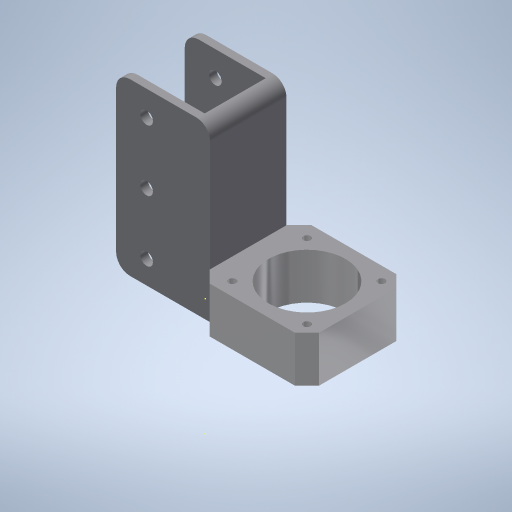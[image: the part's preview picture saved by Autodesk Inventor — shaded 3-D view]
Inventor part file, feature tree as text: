
AUTODESK INVENTOR PART (.ipt)
format: ipt  version: 2024 (Build 280153000, 153)  size: 638,464 bytes
history: native  units: mm
features: extrude x28, sketch x25, projected_geometry x17, fillet x5, chamfer x3
ambient origin geometry x8: Origin, YZ Plane, XZ Plane, XY Plane, X Axis, Y Axis, Z Axis, Center Point
bodies: Solid1 (feature_tree)
feature tree (78):
  extrude  "Extrusion1"  Depth=5.0mm
  fillet  "Fillet1"  Radius=5.0mm
  extrude  "Extrusion2"  Depth=21.1mm
  fillet  "Fillet2"  Radius=3.0mm
  extrude  "Extrusion3"  Depth=3.0mm
  extrude  "Extrusion4"  Depth=31.0mm
  extrude  "Extrusion5"  Depth=31.0mm
  fillet  "Fillet3"  Radius=31.0mm
  extrude  "Extrusion6"  Depth=5.6mm
  fillet  "Fillet4"  Radius=9.8mm
  extrude  "Extrusion7"  Depth=31.0mm TaperAngle=0.0deg
  sketch  "Sketch8"  dims[d14=3.0mm d15=3.0mm]
  extrude  "Extrusion8"  Depth=7.75mm TaperAngle=0.0deg
  extrude  "Extrusion9"  Depth=0.6mm TaperAngle=0.0deg
  extrude  "Extrusion10"  Depth=2.2mm TaperAngle=0.0deg
  extrude  "Extrusion11"  Depth=22.5mm TaperAngle=0.0deg
  extrude  "Extrusion12"  Depth=5.6mm
  extrude  "Extrusion13"  Depth=5.6mm
  extrude  "Extrusion14"  Depth=42.2mm
  chamfer  "Chamfer1"  Distance=6.35mm
  sketch  "Sketch16"  dims[d39=0.5mm d40=22.5mm d41=0.0mm]
  extrude  "Extrusion15"  Depth=98.4mm TaperAngle=0.0deg
  extrude  "Extrusion16"  Depth=16.9926mm TaperAngle=0.0deg
  extrude  "Extrusion17"  Depth=3.9926mm TaperAngle=0.0deg
  extrude  "Extrusion18"  Depth=8.4074mm
  extrude  "Extrusion19"  Depth=3.175mm
  extrude  "Extrusion20"  Depth=39.1mm TaperAngle=0.0deg
  extrude  "Extrusion21"  Depth=39.1mm TaperAngle=0.0deg
  extrude  "Extrusion22"  Depth=25.8mm TaperAngle=0.0deg
  extrude  "Extrusion23"  Depth=51.95mm TaperAngle=0.0deg
  extrude  "Extrusion24"  Depth=10.3886mm
  extrude  "Extrusion25"  Depth=25.4mm
  extrude  "Extrusion26"  Depth=25.4mm
  extrude  "Extrusion27"  Depth=5.75mm
  extrude  "Extrusion28"  Depth=5.75mm
  chamfer  "Chamfer2"  Distance=133.45mm
  chamfer  "Chamfer3"  Distance=6.35mm
  fillet  "Fillet7"  Radius=6.35mm
  sketch  "Sketch1"  dims[d8=5.0mm d9=5.0mm d10=5.0mm]
  sketch  "Sketch7"  dims[d11=21.1mm d12=21.1mm d13=3.0mm]
  projected_geometry  "Projected Loop1"
  sketch  "Sketch9"  dims[d16=3.0mm d17=31.0mm]
  sketch  "Sketch10"  dims[d18=31.0mm d19=31.0mm d20=31.0mm]
  projected_geometry  "Projected Loop2"
  projected_geometry  "Projected Loop3"
  sketch  "Sketch11"  dims[d21=5.6mm d22=5.6mm d23=9.8mm d24=0.0mm]
  sketch  "Sketch12"  dims[d25=0.25mm d26=31.0mm d27=0.0mm]
  projected_geometry  "Projected Loop4"
  projected_geometry  "Projected Loop5"
  sketch  "Sketch13"  dims[d28=0.25mm d29=7.75mm d30=0.0mm]
  projected_geometry  "Projected Loop6"
  projected_geometry  "Projected Loop7"
  sketch  "Sketch14"  dims[d31=32.0mm d33=0.6mm d34=0.0mm]
  sketch  "Sketch15"  dims[d35=22.0mm d37=2.2mm d38=0.0mm]
  projected_geometry  "Projected Loop8"
  projected_geometry  "Projected Loop9"
  projected_geometry  "Projected Loop10"
  projected_geometry  "Projected Loop11"
  sketch  "Sketch17"  dims[d42=0.5mm d43=5.6mm]
  sketch  "Sketch18"  dims[d44=5.6mm d45=5.6mm]
  sketch  "Sketch19"  dims[d46=5.6mm d47=42.2mm d48=6.35mm d49=0.0mm]
  sketch  "Sketch20"  dims[d50=6.35mm d51=98.4mm d52=0.0mm]
  projected_geometry  "Projected Loop12"
  sketch  "Sketch21"  dims[d53=76.85mm d54=0.0mm d55=16.9926mm d56=0.0mm]
  projected_geometry  "Projected Loop13"
  sketch  "Sketch22"  dims[d57=3.9926mm d58=0.0mm d59=3.9926mm d60=0.0mm]
  sketch  "Sketch23"  dims[d61=8.4074mm d62=8.4074mm]
  sketch  "Sketch24"  dims[d63=25.4mm d64=0.0mm d66=3.175mm]
  sketch  "Sketch25"  dims[d68=3.175mm d69=39.1mm d70=0.0mm]
  sketch  "Sketch26"  dims[d71=5.0mm d72=2.0mm d73=45.0deg d74=39.1mm d75=0.0mm]
  projected_geometry  "Projected Loop14"
  sketch  "Sketch27"  dims[d76=12.7mm d77=0.0mm d78=25.8mm d79=0.0mm]
  projected_geometry  "Projected Loop15"
  sketch  "Sketch28"  dims[d80=12.7mm d81=0.0mm d82=51.95mm d83=0.0mm]
  projected_geometry  "Projected Loop16"
  sketch  "Sketch29"  dims[d84=71.05mm d85=0.0mm d86=10.3886mm]
  sketch  "Sketch30"  dims[d87=5.2578mm d88=25.4mm d89=25.4mm d90=5.2578mm d91=5.2578mm d92=133.45mm d93=0.0mm d95=6.35mm d96=6.35mm d97=0.0mm d98=7.6mm d99=0.0mm d100=55.35mm d101=0.0mm d102=194.15mm d103=0.0mm d104=28.6mm d105=0.0mm d107=115.4mm d108=0.0mm d109=10.9mm d110=0.0mm d113=8.25mm d114=2.0mm d115=45.0deg d116=8.25mm d117=2.0mm d118=45.0deg d119=5.75mm]
  projected_geometry  "Projected Loop17"
